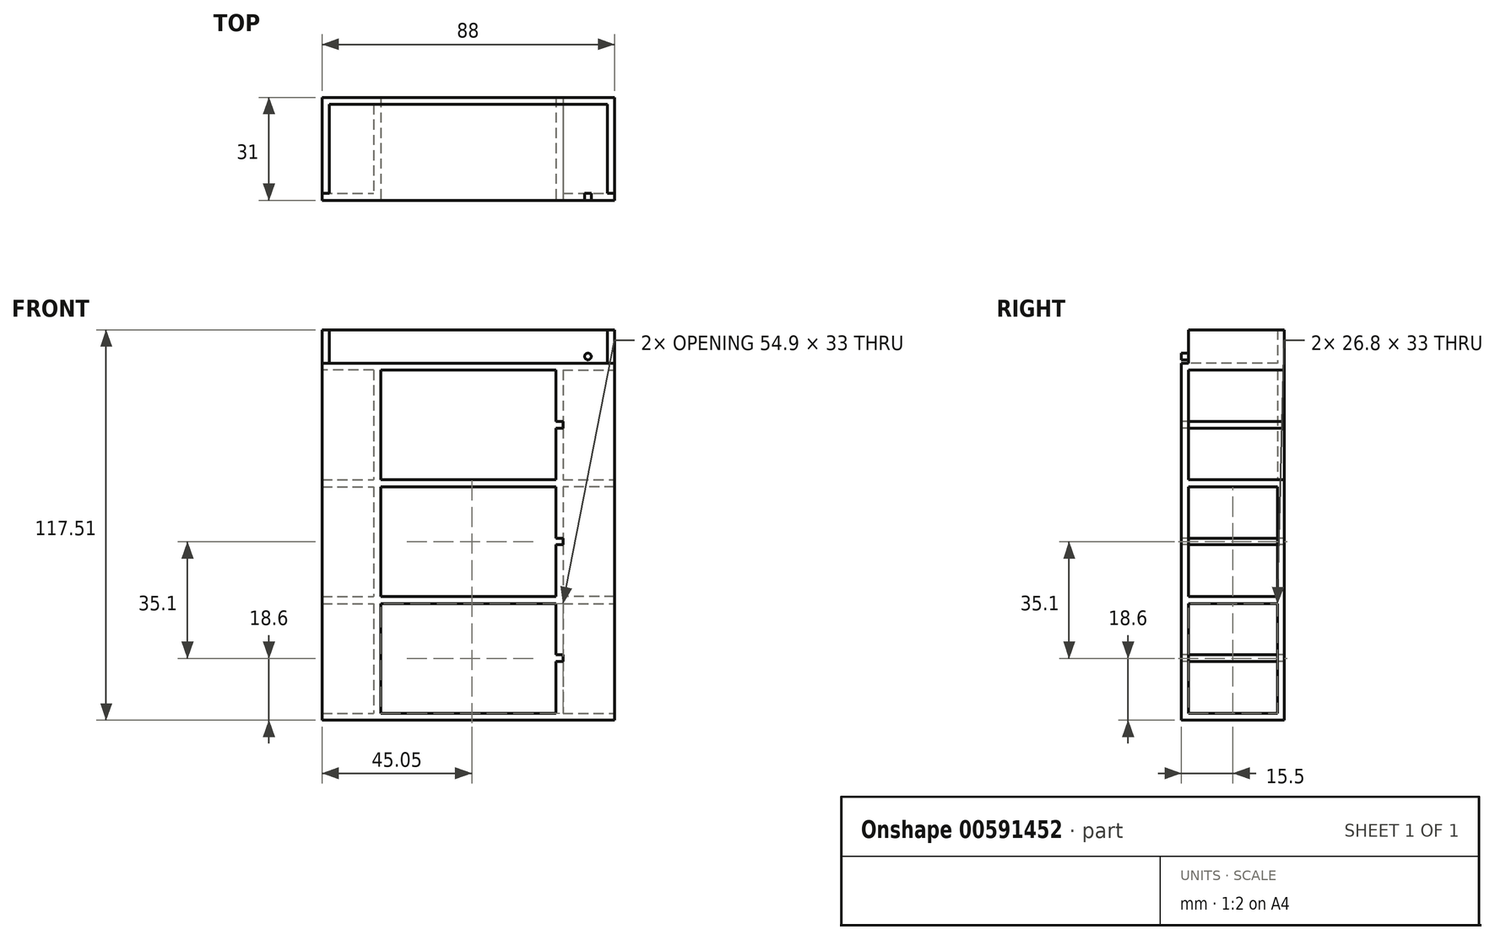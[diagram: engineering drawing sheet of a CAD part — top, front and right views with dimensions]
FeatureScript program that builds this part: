
annotation { "Feature Type Name" : "Feature", "Feature Type Description" : "" }
export const myFeature = defineFeature(function(context is Context, id is Id, definition is map)
    precondition{}
    {
        {
            var Q0;
            Q0=qCreatedBy(makeId("Top.planeOp"),FACE);
            var sketch = newSketch(context, id + "F0", { "sketchPlane" : qUnion([Q0])});
            skLineSegment(sketch, "E0.bottom", {"start": v(-44, 0) * mm, "end": v(44, 0) * mm});
            skLineSegment(sketch, "E0.top", {"start": v(-44, -15.5) * mm, "end": v(44, -15.5) * mm});
            skLineSegment(sketch, "E0.left", {"start": v(-44, 0) * mm, "end": v(-44, -15.5) * mm});
            skLineSegment(sketch, "E0.right", {"start": v(44, 0) * mm, "end": v(44, -15.5) * mm});
            skLineSegment(sketch, "E1.1.0.1", {"start": v(-44, -15.5) * mm, "end": v(-44, -31) * mm});
            skLineSegment(sketch, "E1.1.0.2", {"start": v(-44, -31) * mm, "end": v(44, -31) * mm});
            skLineSegment(sketch, "E1.1.0.3", {"start": v(44, -15.5) * mm, "end": v(44, -31) * mm});
            skLineSegment(sketch, "E1.direction1", {"start": v(-44, 0) * mm, "end": v(-44, -15.5) * mm, "construction": true});
            skSolve(sketch);
        }
        {
            var Q0;
            Q0 = qSketchRegion(id + "F0", true);
            extrude(context, id + "F1", {"entities" : qUnion([Q0]), "oppositeDirection" : true, "depth" : 2.1 * mm, "offsetDistance" : 25 * mm});
        }
        {
            var Q0;
            Q0=makeQuery(id+"F1.opExtrude","CAP_FACE",FACE,{"disambiguationData":[OSD([sQuery(id+"F0.wireOp",EDGE,"E0.bottom"),sQuery(id+"F0.wireOp",EDGE,"E0.left"),sQuery(id+"F0.wireOp",EDGE,"E0.right"),sQuery(id+"F0.wireOp",EDGE,"E1.1.0.1"),sQuery(id+"F0.wireOp",EDGE,"E1.1.0.2"),sQuery(id+"F0.wireOp",EDGE,"E1.1.0.3"),sQuery(id+"F0.wireOp",EDGE,"dMX0KD8X-9XSb-aeHa-tuUe-Ka0AEQhhY9Rm.bottom"),sQuery(id+"F0.wireOp",EDGE,"dMX0KD8X-9XSb-aeHa-tuUe-Ka0AEQhhY9Rm.top"),sQuery(id+"F0.wireOp",EDGE,"POcBFPNy-lRjl-HLuA-zUKZ-1F08yK1WgohE.bottom"),sQuery(id+"F0.wireOp",EDGE,"POcBFPNy-lRjl-HLuA-zUKZ-1F08yK1WgohE.top")])],"isStart":true});
            var sketch = newSketch(context, id + "F2", { "sketchPlane" : qUnion([Q0])});
            skLineSegment(sketch, "E2.bottom", {"start": v(-28.5, 0) * mm, "end": v(-26.4, 0) * mm});
            skLineSegment(sketch, "E2.top", {"start": v(-28.5, -31) * mm, "end": v(-26.4, -31) * mm});
            skLineSegment(sketch, "E2.left", {"start": v(-28.5, 0) * mm, "end": v(-28.5, -31) * mm});
            skLineSegment(sketch, "E2.right", {"start": v(-26.4, 0) * mm, "end": v(-26.4, -31) * mm});
            skLineSegment(sketch, "E3.bottom", {"start": v(26.4, 0) * mm, "end": v(28.5, 0) * mm});
            skLineSegment(sketch, "E3.top", {"start": v(26.4, -31) * mm, "end": v(28.5, -31) * mm});
            skLineSegment(sketch, "E3.left", {"start": v(26.4, 0) * mm, "end": v(26.4, -31) * mm});
            skLineSegment(sketch, "E3.right", {"start": v(28.5, 0) * mm, "end": v(28.5, -31) * mm});
            skLineSegment(sketch, "E4.bottom", {"start": v(-44, 0) * mm, "end": v(-28.5, 0) * mm});
            skLineSegment(sketch, "E4.top", {"start": v(-44, -2.1) * mm, "end": v(-28.5, -2.1) * mm});
            skLineSegment(sketch, "E4.left", {"start": v(-44, 0) * mm, "end": v(-44, -2.1) * mm});
            skLineSegment(sketch, "E4.right", {"start": v(-28.5, 0) * mm, "end": v(-28.5, -2.1) * mm});
            skLineSegment(sketch, "E5.bottom", {"start": v(-44, -28.9) * mm, "end": v(-28.5, -28.9) * mm});
            skLineSegment(sketch, "E5.top", {"start": v(-44, -31) * mm, "end": v(-28.5, -31) * mm});
            skLineSegment(sketch, "E5.left", {"start": v(-44, -28.9) * mm, "end": v(-44, -31) * mm});
            skLineSegment(sketch, "E5.right", {"start": v(-28.5, -28.9) * mm, "end": v(-28.5, -31) * mm});
            skLineSegment(sketch, "E6.bottom", {"start": v(28.5, 0) * mm, "end": v(44, 0) * mm});
            skLineSegment(sketch, "E6.top", {"start": v(28.5, -2.1) * mm, "end": v(44, -2.1) * mm});
            skLineSegment(sketch, "E6.left", {"start": v(28.5, 0) * mm, "end": v(28.5, -2.1) * mm});
            skLineSegment(sketch, "E6.right", {"start": v(44, 0) * mm, "end": v(44, -2.1) * mm});
            skLineSegment(sketch, "E7.bottom", {"start": v(28.5, -31) * mm, "end": v(44, -31) * mm});
            skLineSegment(sketch, "E7.top", {"start": v(28.5, -28.9) * mm, "end": v(44, -28.9) * mm});
            skLineSegment(sketch, "E7.left", {"start": v(28.5, -31) * mm, "end": v(28.5, -28.9) * mm});
            skLineSegment(sketch, "E7.right", {"start": v(44, -31) * mm, "end": v(44, -28.9) * mm});
            skSolve(sketch);
        }
        {
            var Q0;
            Q0 = qSketchRegion(id + "F2", true);
            extrude(context, id + "F3", {"entities" : qUnion([Q0]), "operationType" : NewBodyOperationType.ADD, "depth" : 33 * mm, "offsetDistance" : 25 * mm});
        }
        {
            var Q0;
            Q0=makeQuery(id+"F3.opExtrude","CAP_FACE",FACE,{"disambiguationData":[OSD([sQuery(id+"F2.wireOp",EDGE,"E2.bottom"),sQuery(id+"F2.wireOp",EDGE,"E2.top"),sQuery(id+"F2.wireOp",EDGE,"E2.left"),sQuery(id+"F2.wireOp",EDGE,"E2.right")])],"isStart":false});
            var sketch = newSketch(context, id + "F4", { "sketchPlane" : qUnion([Q0])});
            skLineSegment(sketch, "E8.bottom", {"start": v(-44, 0) * mm, "end": v(44, 0) * mm});
            skLineSegment(sketch, "E8.top", {"start": v(-44, -31) * mm, "end": v(44, -31) * mm});
            skLineSegment(sketch, "E8.left", {"start": v(-44, 0) * mm, "end": v(-44, -31) * mm});
            skLineSegment(sketch, "E8.right", {"start": v(44, 0) * mm, "end": v(44, -31) * mm});
            skSolve(sketch);
        }
        {
            var Q0;
            Q0 = qSketchRegion(id + "F4", true);
            extrude(context, id + "F5", {"entities" : qUnion([Q0]), "operationType" : NewBodyOperationType.ADD, "depth" : 2.1 * mm, "offsetDistance" : 25 * mm});
        }
        {
            var Q0;
            Q0=makeQuery(id+"F5.opExtrude","CAP_FACE",FACE,{"disambiguationData":[OSD([sQuery(id+"F4.wireOp",EDGE,"E8.bottom"),sQuery(id+"F4.wireOp",EDGE,"E8.top"),sQuery(id+"F4.wireOp",EDGE,"E8.left"),sQuery(id+"F4.wireOp",EDGE,"E8.right")])],"isStart":false});
            var sketch = newSketch(context, id + "F6", { "sketchPlane" : qUnion([Q0])});
            skLineSegment(sketch, "E9.bottom", {"start": v(-28.5, 0) * mm, "end": v(-26.4, 0) * mm});
            skLineSegment(sketch, "E9.top", {"start": v(-28.5, -31) * mm, "end": v(-26.4, -31) * mm});
            skLineSegment(sketch, "E9.left", {"start": v(-28.5, 0) * mm, "end": v(-28.5, -31) * mm});
            skLineSegment(sketch, "E9.right", {"start": v(-26.4, 0) * mm, "end": v(-26.4, -31) * mm});
            skLineSegment(sketch, "E10.bottom", {"start": v(26.4, 0) * mm, "end": v(28.5, 0) * mm});
            skLineSegment(sketch, "E10.top", {"start": v(26.4, -31) * mm, "end": v(28.5, -31) * mm});
            skLineSegment(sketch, "E10.left", {"start": v(26.4, 0) * mm, "end": v(26.4, -31) * mm});
            skLineSegment(sketch, "E10.right", {"start": v(28.5, 0) * mm, "end": v(28.5, -31) * mm});
            skLineSegment(sketch, "E11.bottom", {"start": v(-44, 0) * mm, "end": v(-28.5, 0) * mm});
            skLineSegment(sketch, "E11.top", {"start": v(-44, -2.1) * mm, "end": v(-28.5, -2.1) * mm});
            skLineSegment(sketch, "E11.left", {"start": v(-44, 0) * mm, "end": v(-44, -2.1) * mm});
            skLineSegment(sketch, "E11.right", {"start": v(-28.5, 0) * mm, "end": v(-28.5, -2.1) * mm});
            skLineSegment(sketch, "E12.MirrorCS", {"start": v(44, 0) * mm, "end": v(28.5, 0) * mm});
            skLineSegment(sketch, "E13.MirrorCS", {"start": v(44, -2.1) * mm, "end": v(28.5, -2.1) * mm});
            skLineSegment(sketch, "E14.bottom", {"start": v(-44, -28.9) * mm, "end": v(-28.5, -28.9) * mm});
            skLineSegment(sketch, "E14.top", {"start": v(-44, -31) * mm, "end": v(-28.5, -31) * mm});
            skLineSegment(sketch, "E14.left", {"start": v(-44, -28.9) * mm, "end": v(-44, -31) * mm});
            skLineSegment(sketch, "E14.right", {"start": v(-28.5, -28.9) * mm, "end": v(-28.5, -31) * mm});
            skLineSegment(sketch, "E15.MirrorCS", {"start": v(44, -28.9) * mm, "end": v(28.5, -28.9) * mm});
            skLineSegment(sketch, "E16.MirrorCS", {"start": v(44, -31) * mm, "end": v(28.5, -31) * mm});
            skSolve(sketch);
        }
        {
            var Q0;
            Q0 = qSketchRegion(id + "F6", true);
            var Q1;
            {var subQ2=sQuery(id+"F6.wireOp",EDGE,"E15.MirrorCS");Q1=makeQuery(id+"F6.imprint","IMPRINT",FACE,{"disambiguationData":[TD([[makeQuery(id+"F6.imprint","IMPRINT",EDGE,{"derivedFrom":subQ2}),1.0]])]});}
            var Q2;
            {var subQ0=sQuery(id+"F6.wireOp",EDGE,"E12.MirrorCS");Q2=makeQuery(id+"F6.imprint","IMPRINT",FACE,{"disambiguationData":[TD([[makeQuery(id+"F6.imprint","IMPRINT",EDGE,{"derivedFrom":subQ0}),-1.0]])]});}
            extrude(context, id + "F7", {"entities" : qUnion([Q0, Q1, Q2]), "operationType" : NewBodyOperationType.ADD, "depth" : 33 * mm, "offsetDistance" : 25 * mm});
        }
        {
            var Q0;
            Q0=makeQuery(id+"F7.opExtrude","CAP_FACE",FACE,{"disambiguationData":[OSD([sQuery(id+"F6.wireOp",EDGE,"E9.bottom"),sQuery(id+"F6.wireOp",EDGE,"E9.top"),sQuery(id+"F6.wireOp",EDGE,"E9.left"),sQuery(id+"F6.wireOp",EDGE,"E9.right")])],"isStart":false});
            var sketch = newSketch(context, id + "F8", { "sketchPlane" : qUnion([Q0])});
            skLineSegment(sketch, "E17.bottom", {"start": v(-44, 0) * mm, "end": v(44, 0) * mm});
            skLineSegment(sketch, "E17.top", {"start": v(-44, -31) * mm, "end": v(44, -31) * mm});
            skLineSegment(sketch, "E17.left", {"start": v(-44, 0) * mm, "end": v(-44, -31) * mm});
            skLineSegment(sketch, "E17.right", {"start": v(44, 0) * mm, "end": v(44, -31) * mm});
            skSolve(sketch);
        }
        {
            var Q0;
            Q0 = qSketchRegion(id + "F8", true);
            extrude(context, id + "F9", {"entities" : qUnion([Q0]), "operationType" : NewBodyOperationType.ADD, "depth" : 2.2 * mm, "offsetDistance" : 25 * mm});
        }
        {
            var Q0;
            Q0=makeQuery(id+"F9.opExtrude","CAP_FACE",FACE,{"disambiguationData":[OSD([sQuery(id+"F8.wireOp",EDGE,"E17.bottom"),sQuery(id+"F8.wireOp",EDGE,"E17.top"),sQuery(id+"F8.wireOp",EDGE,"E17.left"),sQuery(id+"F8.wireOp",EDGE,"E17.right")])],"isStart":false});
            var sketch = newSketch(context, id + "F10", { "sketchPlane" : qUnion([Q0])});
            skLineSegment(sketch, "E18.bottom", {"start": v(-28.5, 0) * mm, "end": v(-26.4, 0) * mm});
            skLineSegment(sketch, "E18.top", {"start": v(-28.5, -31) * mm, "end": v(-26.4, -31) * mm});
            skLineSegment(sketch, "E18.left", {"start": v(-28.5, 0) * mm, "end": v(-28.5, -31) * mm});
            skLineSegment(sketch, "E18.right", {"start": v(-26.4, 0) * mm, "end": v(-26.4, -31) * mm});
            skLineSegment(sketch, "E19.bottom", {"start": v(26.4, 0) * mm, "end": v(28.5, 0) * mm});
            skLineSegment(sketch, "E19.top", {"start": v(26.4, -31) * mm, "end": v(28.5, -31) * mm});
            skLineSegment(sketch, "E19.left", {"start": v(26.4, 0) * mm, "end": v(26.4, -31) * mm});
            skLineSegment(sketch, "E19.right", {"start": v(28.5, 0) * mm, "end": v(28.5, -31) * mm});
            skLineSegment(sketch, "E20.bottom", {"start": v(-44, 0) * mm, "end": v(-28.5, 0) * mm});
            skLineSegment(sketch, "E20.top", {"start": v(-44, -2.1) * mm, "end": v(-28.5, -2.1) * mm});
            skLineSegment(sketch, "E20.left", {"start": v(-44, 0) * mm, "end": v(-44, -2.1) * mm});
            skLineSegment(sketch, "E20.right", {"start": v(-28.5, 0) * mm, "end": v(-28.5, -2.1) * mm});
            skLineSegment(sketch, "E21.bottom", {"start": v(28.5, -28.9) * mm, "end": v(44, -28.9) * mm});
            skLineSegment(sketch, "E21.top", {"start": v(28.5, -31) * mm, "end": v(44, -31) * mm});
            skLineSegment(sketch, "E21.left", {"start": v(28.5, -28.9) * mm, "end": v(28.5, -31) * mm});
            skLineSegment(sketch, "E21.right", {"start": v(44, -28.9) * mm, "end": v(44, -31) * mm});
            skLineSegment(sketch, "E22.bottom", {"start": v(-28.5, -28.9) * mm, "end": v(-44, -28.9) * mm});
            skLineSegment(sketch, "E22.top", {"start": v(-28.5, -31) * mm, "end": v(-44, -31) * mm});
            skLineSegment(sketch, "E22.left", {"start": v(-28.5, -28.9) * mm, "end": v(-28.5, -31) * mm});
            skLineSegment(sketch, "E22.right", {"start": v(-44, -28.9) * mm, "end": v(-44, -31) * mm});
            skLineSegment(sketch, "E23.bottom", {"start": v(44, -28.9) * mm, "end": v(41.9, -28.9) * mm});
            skLineSegment(sketch, "E24", {"start": v(41.9, -28.9) * mm, "end": v(41.9, 0) * mm});
            skLineSegment(sketch, "E25", {"start": v(44, -28.9) * mm, "end": v(44, 0) * mm});
            skLineSegment(sketch, "E26", {"start": v(44, 0) * mm, "end": v(41.9, 0) * mm});
            skSolve(sketch);
        }
        {
            var Q0;
            Q0=makeQuery(id+"F10.imprint","IMPRINT",FACE,{"disambiguationData":[TD([[makeQuery(id+"F10.imprint","IMPRINT",EDGE,{"derivedFrom":sQuery(id+"F10.wireOp",EDGE,"E20.bottom")}),-1.0]])]});
            var Q1;
            Q1=makeQuery(id+"F10.imprint","IMPRINT",FACE,{"disambiguationData":[TD([[makeQuery(id+"F10.imprint","IMPRINT",EDGE,{"derivedFrom":sQuery(id+"F10.wireOp",EDGE,"E21.bottom")}),-1.0]])]});
            var Q2;
            Q2=makeQuery(id+"F10.imprint","IMPRINT",FACE,{"disambiguationData":[TD([[makeQuery(id+"F10.imprint","IMPRINT",EDGE,{"derivedFrom":sQuery(id+"F10.wireOp",EDGE,"E22.bottom")}),1.0]])]});
            var Q3;
            Q3=makeQuery(id+"F10.imprint","IMPRINT",FACE,{"disambiguationData":[TD([[makeQuery(id+"F10.imprint","IMPRINT",EDGE,{"derivedFrom":sQuery(id+"F10.wireOp",EDGE,"E18.bottom")}),-1.0]])]});
            var Q4;
            Q4=makeQuery(id+"F10.imprint","IMPRINT",FACE,{"disambiguationData":[TD([[makeQuery(id+"F10.imprint","IMPRINT",EDGE,{"derivedFrom":sQuery(id+"F10.wireOp",EDGE,"E19.bottom")}),-1.0]])]});
            var Q5;
            Q5=makeQuery(id+"F10.imprint","IMPRINT",FACE,{"disambiguationData":[TD([[makeQuery(id+"F10.imprint","IMPRINT",EDGE,{"derivedFrom":sQuery(id+"F10.wireOp",EDGE,"E23.bottom")}),-1.0]])]});
            extrude(context, id + "F11", {"entities" : qUnion([Q0, Q1, Q2, Q3, Q4, Q5]), "operationType" : NewBodyOperationType.ADD, "depth" : 33 * mm, "offsetDistance" : 25 * mm});
        }
        {
            var Q0;
            Q0=makeQuery(id+"F11.opExtrude","CAP_FACE",FACE,{"disambiguationData":[OSD([sQuery(id+"F10.wireOp",EDGE,"E18.bottom"),sQuery(id+"F10.wireOp",EDGE,"E18.top"),sQuery(id+"F10.wireOp",EDGE,"E18.left"),sQuery(id+"F10.wireOp",EDGE,"E18.right")])],"isStart":false});
            var sketch = newSketch(context, id + "F12", { "sketchPlane" : qUnion([Q0])});
            skLineSegment(sketch, "E27.bottom", {"start": v(-44, 0) * mm, "end": v(44, 0) * mm});
            skLineSegment(sketch, "E27.top", {"start": v(-44, -31) * mm, "end": v(44, -31) * mm});
            skLineSegment(sketch, "E27.left", {"start": v(-44, 0) * mm, "end": v(-44, -31) * mm});
            skLineSegment(sketch, "E27.right", {"start": v(44, 0) * mm, "end": v(44, -31) * mm});
            skSolve(sketch);
        }
        {
            var Q0;
            Q0 = qSketchRegion(id + "F12", true);
            extrude(context, id + "F13", {"entities" : qUnion([Q0]), "operationType" : NewBodyOperationType.ADD, "depth" : 2.1 * mm, "offsetDistance" : 25 * mm});
        }
        {
            var Q0;
            Q0=makeQuery(id+"F13.opExtrude","CAP_FACE",FACE,{"disambiguationData":[OSD([sQuery(id+"F12.wireOp",EDGE,"E27.bottom"),sQuery(id+"F12.wireOp",EDGE,"E27.top"),sQuery(id+"F12.wireOp",EDGE,"E27.left"),sQuery(id+"F12.wireOp",EDGE,"E27.right")])],"isStart":false});
            var sketch = newSketch(context, id + "F14", { "sketchPlane" : qUnion([Q0])});
            skLineSegment(sketch, "E28.bottom", {"start": v(-44, 0) * mm, "end": v(44, 0) * mm});
            skLineSegment(sketch, "E28.top", {"start": v(-44, -31) * mm, "end": v(44, -31) * mm});
            skLineSegment(sketch, "E28.left", {"start": v(-44, 0) * mm, "end": v(-44, -31) * mm});
            skLineSegment(sketch, "E28.right", {"start": v(44, 0) * mm, "end": v(44, -31) * mm});
            skLineSegment(sketch, "E29.bottom", {"start": v(-41.9, -2.1) * mm, "end": v(41.9, -2.1) * mm});
            skLineSegment(sketch, "E29.top", {"start": v(-41.9, -28.9) * mm, "end": v(41.9, -28.9) * mm});
            skLineSegment(sketch, "E29.left", {"start": v(-41.9, -2.1) * mm, "end": v(-41.9, -28.9) * mm});
            skLineSegment(sketch, "E29.right", {"start": v(41.9, -2.1) * mm, "end": v(41.9, -28.9) * mm});
            skSolve(sketch);
        }
        {
            var Q0;
            Q0 = qSketchRegion(id + "F14", true);
            extrude(context, id + "F15", {"entities" : qUnion([Q0]), "operationType" : NewBodyOperationType.ADD, "depth" : 10 * mm, "offsetDistance" : 25 * mm});
        }
        {
            var Q0;
            Q0=makeQuery(id+"F15.boolean.opBoolean","MERGE",FACE,{"derivedFrom":[makeQuery(id+"F13.boolean.opBoolean","MERGE",FACE,{"derivedFrom":[makeQuery(id+"F11.boolean.opBoolean","MERGE",FACE,{"derivedFrom":[makeQuery(id+"F9.boolean.opBoolean","MERGE",FACE,{"derivedFrom":[makeQuery(id+"F7.boolean.opBoolean","MERGE",FACE,{"derivedFrom":[makeQuery(id+"F5.boolean.opBoolean","MERGE",FACE,{"derivedFrom":[makeQuery(id+"F3.boolean.opBoolean","MERGE",FACE,{"derivedFrom":[makeQuery(id+"F1.opExtrude","SWEPT_FACE",FACE,{"disambiguationData":[OSD([sQuery(id+"F0.wireOp",EDGE,"E1.1.0.2")])]}),makeQuery(id+"F3.opExtrude","SWEPT_FACE",FACE,{"disambiguationData":[OSD([sQuery(id+"F2.wireOp",EDGE,"E2.top"),sQuery(id+"F2.wireOp",EDGE,"E5.top")])]}),makeQuery(id+"F3.opExtrude","SWEPT_FACE",FACE,{"disambiguationData":[OSD([sQuery(id+"F2.wireOp",EDGE,"E3.top"),sQuery(id+"F2.wireOp",EDGE,"E7.bottom")])]})]}),makeQuery(id+"F5.opExtrude","SWEPT_FACE",FACE,{"disambiguationData":[OSD([sQuery(id+"F4.wireOp",EDGE,"E8.top")])]})]}),makeQuery(id+"F7.opExtrude","SWEPT_FACE",FACE,{"disambiguationData":[OSD([sQuery(id+"F6.wireOp",EDGE,"E9.top"),sQuery(id+"F6.wireOp",EDGE,"E14.top")])]}),makeQuery(id+"F7.opExtrude","SWEPT_FACE",FACE,{"disambiguationData":[OSD([sQuery(id+"F6.wireOp",EDGE,"E10.top"),sQuery(id+"F6.wireOp",EDGE,"E16.MirrorCS")])]})]}),makeQuery(id+"F9.opExtrude","SWEPT_FACE",FACE,{"disambiguationData":[OSD([sQuery(id+"F8.wireOp",EDGE,"E17.top")])]})]}),makeQuery(id+"F11.opExtrude","SWEPT_FACE",FACE,{"disambiguationData":[OSD([sQuery(id+"F10.wireOp",EDGE,"E18.top"),sQuery(id+"F10.wireOp",EDGE,"E22.top")])]}),makeQuery(id+"F11.opExtrude","SWEPT_FACE",FACE,{"disambiguationData":[OSD([sQuery(id+"F10.wireOp",EDGE,"E19.top"),sQuery(id+"F10.wireOp",EDGE,"E21.top")])]})]}),makeQuery(id+"F13.opExtrude","SWEPT_FACE",FACE,{"disambiguationData":[OSD([sQuery(id+"F12.wireOp",EDGE,"E27.top")])]})]}),makeQuery(id+"F15.opExtrude","SWEPT_FACE",FACE,{"disambiguationData":[OSD([sQuery(id+"F14.wireOp",EDGE,"E28.top")])]})]});
            var sketch = newSketch(context, id + "F16", { "sketchPlane" : qUnion([Q0])});
            skLineSegment(sketch, "E30.bottom", {"start": v(-44, 105.4) * mm, "end": v(44, 105.4) * mm});
            skLineSegment(sketch, "E30.top", {"start": v(-44, 103.31) * mm, "end": v(44, 103.31) * mm});
            skLineSegment(sketch, "E30.left", {"start": v(-44, 105.4) * mm, "end": v(-44, 103.31) * mm});
            skLineSegment(sketch, "E30.right", {"start": v(44, 105.4) * mm, "end": v(44, 103.31) * mm});
            skCircle(sketch, "E31", {"center": v(-36, 107.4) * mm, "radius": 1 * mm});
            skCircle(sketch, "E32.MirrorC", {"center": v(36, 107.4) * mm, "radius": 1 * mm});
            skSolve(sketch);
        }
        {
            var Q0;
            Q0=makeQuery(id+"F16.imprint","IMPRINT",FACE,{"disambiguationData":[TD([[makeQuery(id+"F16.imprint","IMPRINT",EDGE,{"derivedFrom":sQuery(id+"F16.wireOp",EDGE,"E31")}),1.0]])]});
            var Q1;
            Q1=makeQuery(id+"F16.imprint","IMPRINT",FACE,{"disambiguationData":[TD([[makeQuery(id+"F16.imprint","IMPRINT",EDGE,{"derivedFrom":sQuery(id+"F16.wireOp",EDGE,"E32.MirrorC")}),-1.0]])]});
            extrude(context, id + "F17", {"entities" : qUnion([Q0, Q1]), "operationType" : NewBodyOperationType.REMOVE, "oppositeDirection" : true, "depth" : 2.1 * mm, "offsetDistance" : 25 * mm});
        }
        {
            var Q0;
            Q0=makeQuery(id+"F11.opExtrude","SWEPT_FACE",FACE,{"disambiguationData":[OSD([sQuery(id+"F10.wireOp",EDGE,"E19.left")])]});
            var sketch = newSketch(context, id + "F18", { "sketchPlane" : qUnion([Q0])});
            skLineSegment(sketch, "E33.bottom", {"start": v(0, 87.81) * mm, "end": v(31, 87.81) * mm});
            skLineSegment(sketch, "E33.top", {"start": v(0, 85.81) * mm, "end": v(31, 85.81) * mm});
            skLineSegment(sketch, "E33.left", {"start": v(0, 87.81) * mm, "end": v(0, 85.81) * mm});
            skLineSegment(sketch, "E33.right", {"start": v(31, 87.81) * mm, "end": v(31, 85.81) * mm});
            skLineSegment(sketch, "E34.1.0.0", {"start": v(0, 52.7) * mm, "end": v(31, 52.7) * mm});
            skLineSegment(sketch, "E34.1.0.1", {"start": v(0, 50.7) * mm, "end": v(31, 50.7) * mm});
            skLineSegment(sketch, "E34.2.0.0", {"start": v(0, 17.6) * mm, "end": v(31, 17.6) * mm});
            skLineSegment(sketch, "E34.2.0.1", {"start": v(0, 15.6) * mm, "end": v(31, 15.6) * mm});
            skLineSegment(sketch, "E34.direction1", {"start": v(0, 85.81) * mm, "end": v(0, 50.7) * mm, "construction": true});
            skLineSegment(sketch, "E35", {"start": v(0, 52.7) * mm, "end": v(0, 50.7) * mm});
            skLineSegment(sketch, "E36", {"start": v(31, 52.7) * mm, "end": v(31, 50.7) * mm});
            skLineSegment(sketch, "E37", {"start": v(0, 17.6) * mm, "end": v(0, 15.6) * mm});
            skLineSegment(sketch, "E38", {"start": v(31, 17.6) * mm, "end": v(31, 15.6) * mm});
            skSolve(sketch);
        }
        {
            var Q0;
            Q0 = qSketchRegion(id + "F18", true);
            extrude(context, id + "F19", {"entities" : qUnion([Q0]), "operationType" : NewBodyOperationType.REMOVE, "oppositeDirection" : true, "depth" : 2.1 * mm, "offsetDistance" : 25 * mm});
        }
    });
